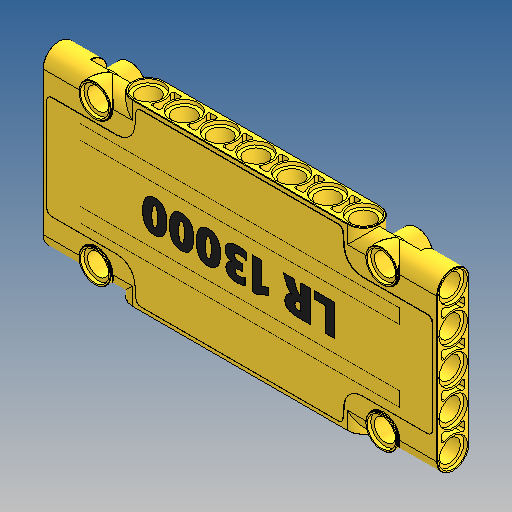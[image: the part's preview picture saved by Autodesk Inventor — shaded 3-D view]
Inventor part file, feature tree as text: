
AUTODESK INVENTOR PART (.ipt)
format: ipt  version: 2025 (Build 290162010, 162A)  size: 1,354,240 bytes
history: native  units: in
note: dims shown in document units (in); Inventor stores cm internally (conversion verified against a paired STEP export)
features: extrude x18, sketch x13, mirror x3, plane x1, fillet x1
ambient origin geometry x8: Origin, YZ Plane, XZ Plane, XY Plane, X Axis, Y Axis, Z Axis, Center Point
bodies: Solid1 (feature_tree)
feature tree (36):
  extrude  "Extrusion1"  Depth=0.189in
  sketch  "Sketch3"  dims[d6=0.189in d7=0.252in]
  extrude  "Extrusion2"  Depth=0.0315in
  extrude  "Extrusion3"  TaperAngle=0.0deg  [1 undecoded]
  extrude  "Extrusion4"  Depth=0.252in
  plane  "Work Plane1"
  extrude  "Extrusion5"  Depth=1.5748in
  sketch  "Sketch5"  dims[d12=0.3937in d14=0.3937in d16=0.2835in]
  extrude  "Extrusion6"  Depth=0.2835in
  extrude  "Extrusion7"  Depth=0.0315in
  extrude  "Extrusion10"  Depth=0.2205in TaperAngle=0.0deg
  extrude  "Extrusion8"  Depth=0.189in
  extrude  "Extrusion9"  Depth=0.0315in TaperAngle=0.0deg
  mirror  "Mirror1"
  mirror  "Mirror2"
  sketch  "Sketch8"  dims[d22=-0.1417in d23=0.189in]
  extrude  "Extrusion11"  Depth=0.189in
  extrude  "Extrusion12"  Depth=0.2677in
  extrude  "Extrusion13"  Depth=0.2677in TaperAngle=0.0deg
  sketch  "Sketch9"  dims[d24=0.2835in d25=0.0315in d26=0.0in]
  extrude  "Extrusion14"  Depth=0.252in
  extrude  "Extrusion16"  Depth=0.0315in
  mirror  "Mirror3"
  extrude  "Extrusion15"  TaperAngle=0.0deg  [1 undecoded]
  fillet  "Fillet1"  Radius=0.252in
  extrude  "Extrusion17"  Depth=0.0315in
  extrude  "Extrusion18"  TaperAngle=0.0deg  [1 undecoded]
  sketch  "Sketch2"  dims[d2=0.2835in d3=0.0315in]
  sketch  "Skizze - Rechteckige Anordnung1"  dims[d0=0.315in d1=0.189in]
  sketch  "Sketch4"  dims[d8=45.0deg d9=1.5748in d11=0.315in]
  sketch  "Sketch6"  dims[d17=0.0in d18=0.0315in]
  sketch  "Sketch7"  dims[d19=0.0in d20=0.2205in d21=0.0in]
  sketch  "Sketch10"  dims[d27=0.2835in d28=0.189in]
  sketch  "Skizze - Rechteckige Anordnung2"  dims[d4=3.4646in d5=0.0in]
  sketch  "Skizze11"  dims[d29=1.2598in d30=0.2677in d31=0.0472in]
  sketch  "Skizze12"  dims[d32=0.0in d33=0.0in d34=0.2677in d35=0.0in d36=0.252in d37=0.0315in d38=0.0in d39=0.252in d40=0.0315in d41=0.0in d42=0.0315in d43=0.2205in d44=0.0in d45=0.2835in d46=1.8898in d47=0.189in d48=0.1417in d49=0.1417in d50=0.0in d51=0.0in d52=0.1417in d53=0.0in d54=0.315in d55=0.0in d56=0.252in d57=0.0315in d58=0.0in d59=2.8031in d60=0.126in d61=0.5039in d62=0.0079in d63=0.0in d64=45.0deg d65=2.3622in d67=0.315in d68=0.3937in d70=0.3937in d72=0.2205in d73=0.0in d74=0.0039in d75=0.0157in d76=0.4528in d77=0.0394in d78=0.0394in d79=0.8268in d80=0.6528in d81=0.1575in d82=0.0394in d83=0.0039in d84=0.0in d85=0.0004in d86=0.0in]
note: 3 required parameter values undecoded (feature->parameter linkage not recoverable at this tier; creation-order binding heuristic only, values carry confidence <= 0.55)
